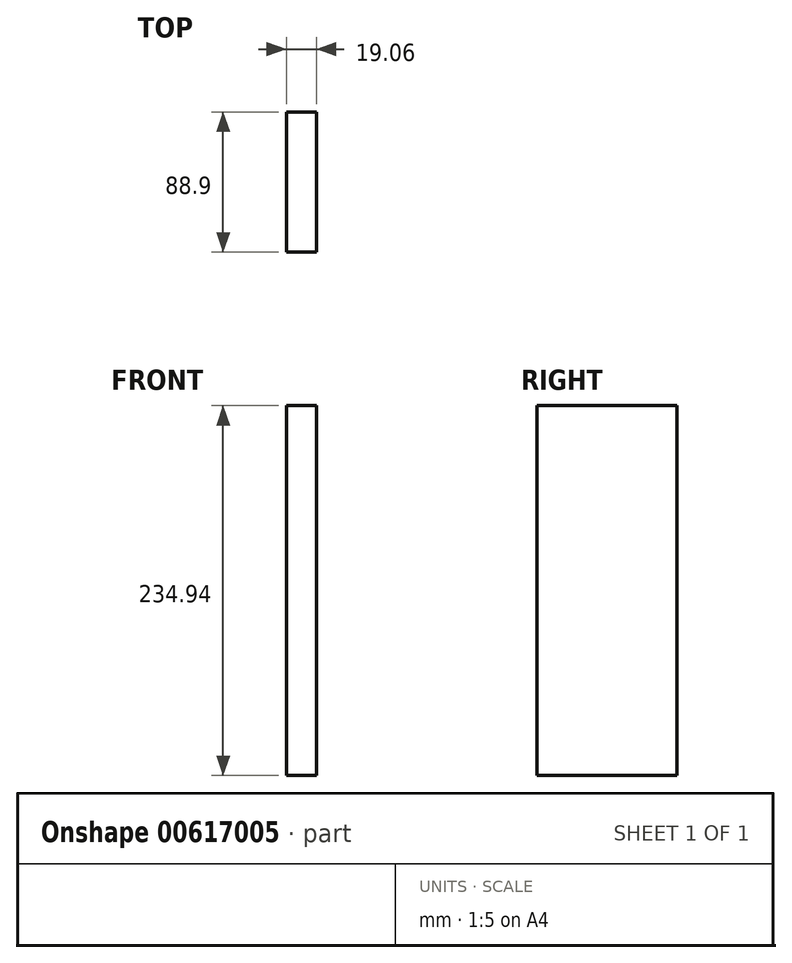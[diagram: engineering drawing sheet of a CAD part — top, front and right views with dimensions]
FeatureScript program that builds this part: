
annotation { "Feature Type Name" : "Feature", "Feature Type Description" : "" }
export const myFeature = defineFeature(function(context is Context, id is Id, definition is map)
    precondition{}
    {
        {
            var Q0;
            Q0=qCreatedBy(makeId("Front.planeOp"),FACE);
            var sketch = newSketch(context, id + "F0", { "sketchPlane" : qUnion([Q0])});
            skLineSegment(sketch, "E0.bottom", {"start": v(9.52, 117.47) * mm, "end": v(-9.53, 117.47) * mm});
            skLineSegment(sketch, "E0.top", {"start": v(9.53, -117.48) * mm, "end": v(-9.52, -117.48) * mm});
            skLineSegment(sketch, "E0.left", {"start": v(9.52, 117.47) * mm, "end": v(9.53, -117.48) * mm});
            skLineSegment(sketch, "E0.right", {"start": v(-9.53, 117.47) * mm, "end": v(-9.52, -117.48) * mm});
            skPoint(sketch, "E0.middle", {"position": v(0, 0) * mm});
            skSolve(sketch);
        }
        {
            var Q0;
            Q0=makeQuery(id+"F0.imprint","IMPRINT",FACE,{"disambiguationData":[TD([[makeQuery(id+"F0.imprint","IMPRINT",EDGE,{"derivedFrom":sQuery(id+"F0.wireOp",EDGE,"E0.bottom")}),1.0]])]});
            extrude(context, id + "F1", {"entities" : qUnion([Q0]), "depth" : 88.9 * mm, "offsetDistance" : 25.4 * mm});
        }
    });
